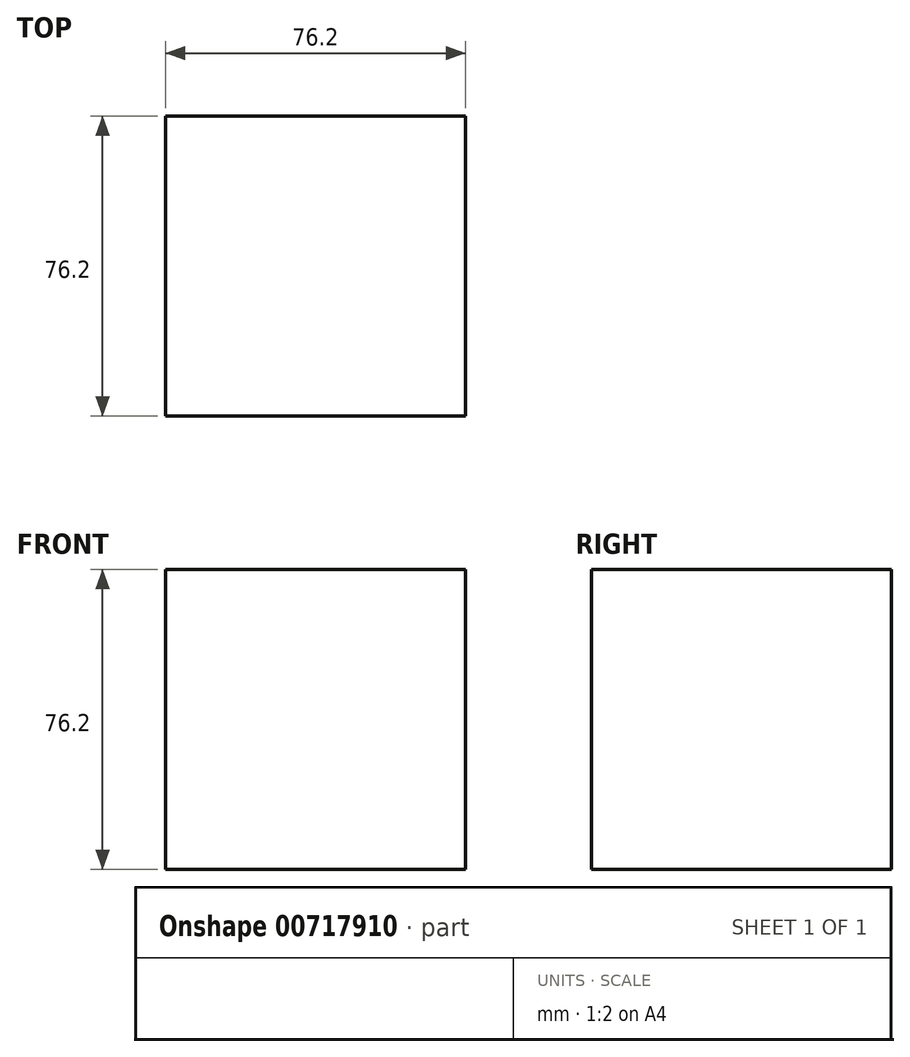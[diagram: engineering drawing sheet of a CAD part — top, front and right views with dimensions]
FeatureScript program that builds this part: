
annotation { "Feature Type Name" : "Feature", "Feature Type Description" : "" }
export const myFeature = defineFeature(function(context is Context, id is Id, definition is map)
    precondition{}
    {
        {
            var Q0;
            Q0=qCreatedBy(makeId("Front.planeOp"),FACE);
            var sketch = newSketch(context, id + "F0", { "sketchPlane" : qUnion([Q0])});
            skLineSegment(sketch, "E0.bottom", {"start": v(-19.8, 22.12) * mm, "end": v(56.4, 22.12) * mm});
            skLineSegment(sketch, "E0.top", {"start": v(-19.8, -54.08) * mm, "end": v(56.4, -54.08) * mm});
            skLineSegment(sketch, "E0.left", {"start": v(-19.8, 22.12) * mm, "end": v(-19.8, -54.08) * mm});
            skLineSegment(sketch, "E0.right", {"start": v(56.4, 22.12) * mm, "end": v(56.4, -54.08) * mm});
            skSolve(sketch);
        }
        {
            var Q0;
            Q0=makeQuery(id+"F0.imprint","IMPRINT",FACE,{"disambiguationData":[TD([[makeQuery(id+"F0.imprint","IMPRINT",EDGE,{"derivedFrom":sQuery(id+"F0.wireOp",EDGE,"E0.bottom")}),-1.0]])]});
            extrude(context, id + "F1", {"entities" : qUnion([Q0]), "depth" : 76.2 * mm, "offsetDistance" : 25.4 * mm});
        }
    });
